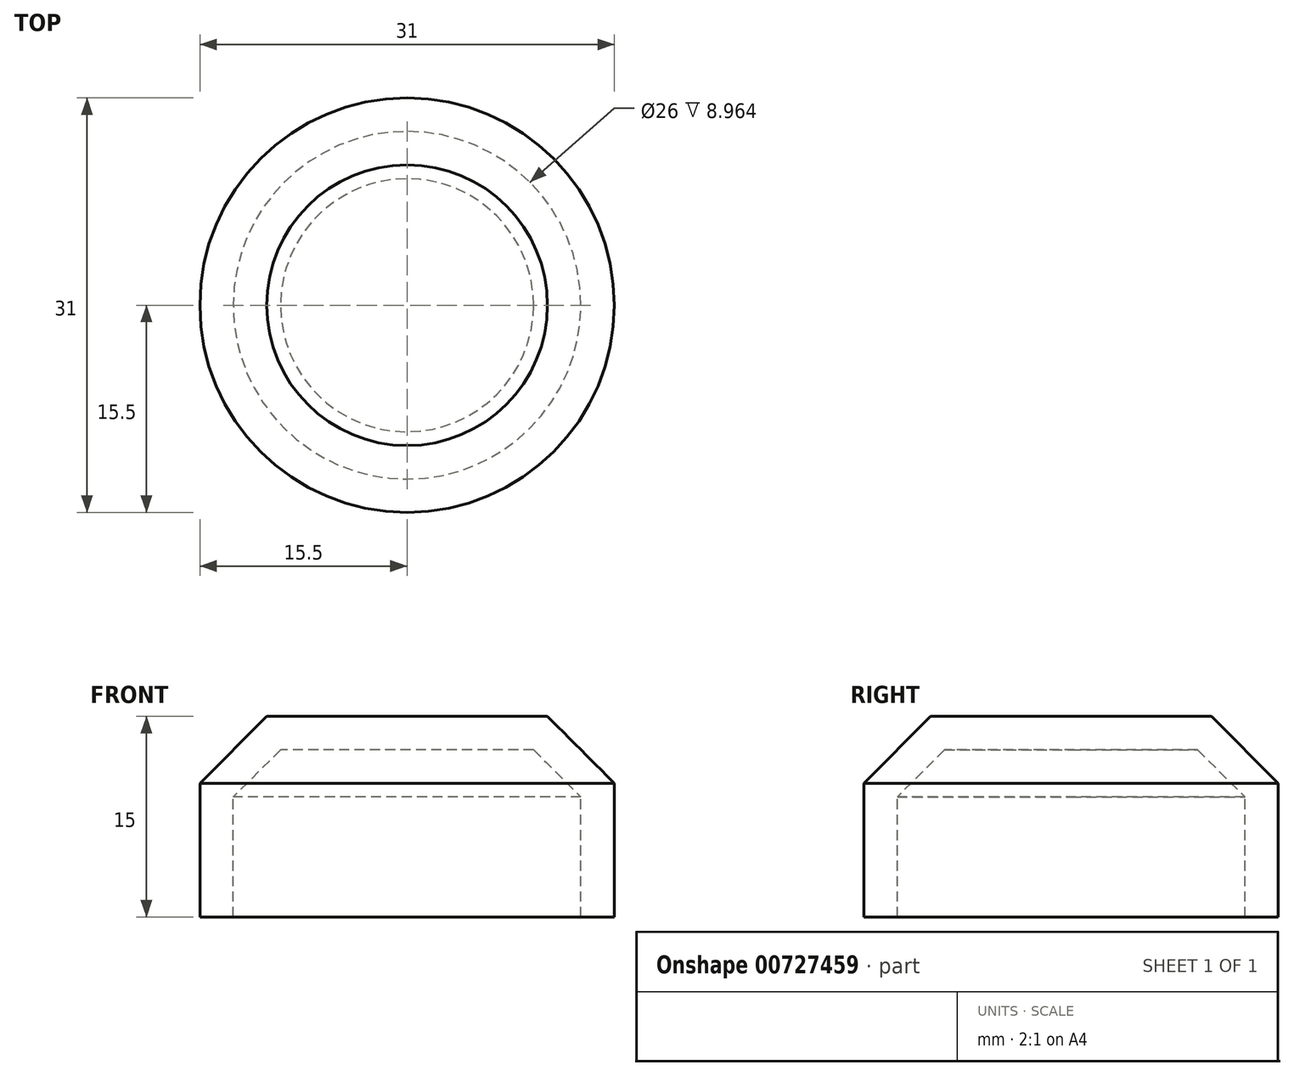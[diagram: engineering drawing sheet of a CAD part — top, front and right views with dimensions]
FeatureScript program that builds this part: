
annotation { "Feature Type Name" : "Feature", "Feature Type Description" : "" }
export const myFeature = defineFeature(function(context is Context, id is Id, definition is map)
    precondition{}
    {
        {
            var Q0;
            Q0=qCreatedBy(makeId("Right.planeOp"),FACE);
            var sketch = newSketch(context, id + "F0", { "sketchPlane" : qUnion([Q0])});
            skLineSegment(sketch, "E0", {"start": v(-15.5, 0) * mm, "end": v(-15.5, 10) * mm});
            skLineSegment(sketch, "E1", {"start": v(-15.5, 10) * mm, "end": v(-10.5, 15) * mm});
            skLineSegment(sketch, "E2", {"start": v(-10.5, 15) * mm, "end": v(0, 15) * mm});
            skLineSegment(sketch, "E3.0", {"start": v(-9.46, 12.5) * mm, "end": v(0, 12.5) * mm});
            skLineSegment(sketch, "E3.1", {"start": v(-13, 8.96) * mm, "end": v(-9.46, 12.5) * mm});
            skLineSegment(sketch, "E3.2", {"start": v(-13, 0) * mm, "end": v(-13, 8.96) * mm});
            skLineSegment(sketch, "E4", {"start": v(-15.5, 0) * mm, "end": v(-13, 0) * mm});
            skLineSegment(sketch, "E5", {"start": v(0, 12.5) * mm, "end": v(0, 15) * mm});
            skLineSegment(sketch, "E6", {"start": v(0, 33.28) * mm, "end": v(0, -9.62) * mm, "construction": true});
            skSolve(sketch);
        }
        {
            var Q0;
            Q0 = qSketchRegion(id + "F0", true);
            var Q1;
            Q1=sQuery(id+"F0.wireOp",EDGE,"E6");
            revolve(context, id + "F1", {"surfaceOperationType" : NewSurfaceOperationType.NEW, "entities" : qUnion([Q0]), "axis" : qUnion([Q1]), "revolveType" : RevolveType.FULL});
        }
    });
